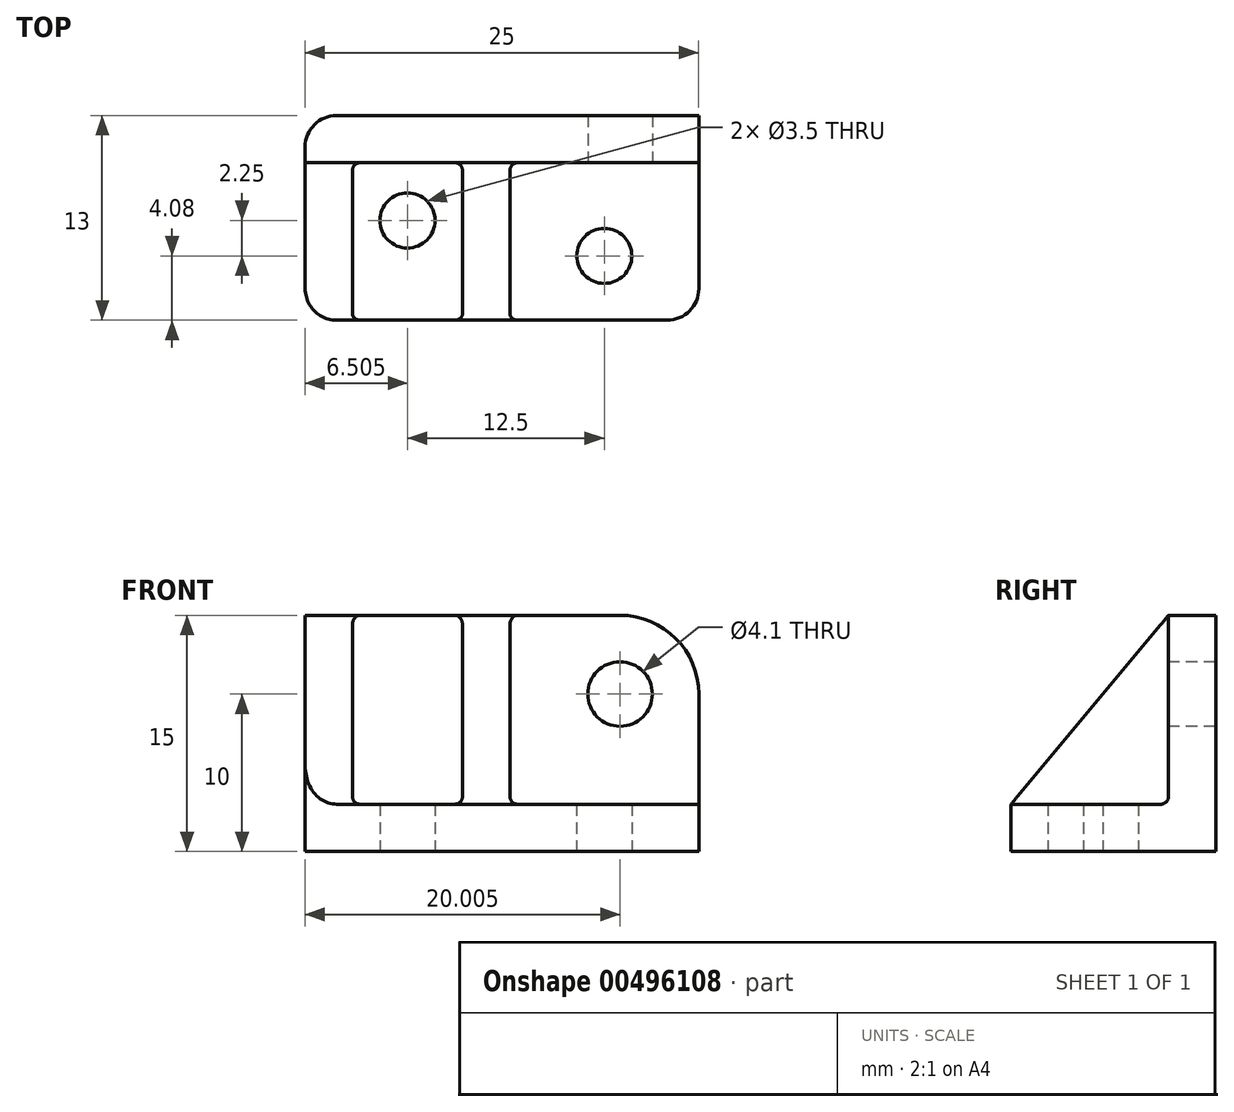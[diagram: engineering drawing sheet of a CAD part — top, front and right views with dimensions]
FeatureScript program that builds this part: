
annotation { "Feature Type Name" : "Feature", "Feature Type Description" : "" }
export const myFeature = defineFeature(function(context is Context, id is Id, definition is map)
    precondition{}
    {
        {
            var Q0;
            Q0=qCreatedBy(makeId("Top.planeOp"),FACE);
            var sketch = newSketch(context, id + "F0", { "sketchPlane" : qUnion([Q0])});
            skLineSegment(sketch, "E0.bottom", {"start": v(-68.38, 21.24) * mm, "end": v(-43.38, 21.24) * mm});
            skLineSegment(sketch, "E0.top", {"start": v(-68.38, 8.24) * mm, "end": v(-43.38, 8.24) * mm});
            skLineSegment(sketch, "E0.left", {"start": v(-68.38, 21.24) * mm, "end": v(-68.38, 8.24) * mm});
            skLineSegment(sketch, "E0.right", {"start": v(-43.38, 21.24) * mm, "end": v(-43.38, 8.24) * mm});
            skLineSegment(sketch, "E1", {"start": v(-68.38, 18.24) * mm, "end": v(-43.38, 18.24) * mm});
            skLineSegment(sketch, "E2", {"start": v(-65.38, 18.24) * mm, "end": v(-65.38, 8.24) * mm});
            skLineSegment(sketch, "E3", {"start": v(-58.38, 18.24) * mm, "end": v(-58.38, 8.24) * mm});
            skLineSegment(sketch, "E4", {"start": v(-55.38, 18.24) * mm, "end": v(-55.38, 8.24) * mm});
            skLineSegment(sketch, "E5", {"start": v(-68.38, 15.74) * mm, "end": v(-43.38, 11.24) * mm, "construction": true});
            skPoint(sketch, "E6", {"position": v(-61.88, 14.57) * mm});
            skPoint(sketch, "E7", {"position": v(-49.38, 12.32) * mm});
            skCircle(sketch, "E8", {"center": v(-61.88, 14.57) * mm, "radius": 1.75 * mm});
            skCircle(sketch, "E9", {"center": v(-49.38, 12.32) * mm, "radius": 1.75 * mm});
            skSolve(sketch);
        }
        {
            var Q0;
            {var subQ0=sQuery(id+"F0.wireOp",EDGE,"E0.bottom");Q0=makeQuery(id+"F0.imprint","IMPRINT",FACE,{"disambiguationData":[TD([[makeQuery(id+"F0.imprint","IMPRINT",EDGE,{"derivedFrom":subQ0}),-1.0]])]});}
            var Q1;
            {var subQ3=sQuery(id+"F0.wireOp",EDGE,"E2");Q1=makeQuery(id+"F0.imprint","IMPRINT",FACE,{"disambiguationData":[TD([[makeQuery(id+"F0.imprint","IMPRINT",EDGE,{"derivedFrom":subQ3}),-1.0]])]});}
            var Q2;
            {var subQ0=sQuery(id+"F0.wireOp",EDGE,"E3");Q2=makeQuery(id+"F0.imprint","IMPRINT",FACE,{"disambiguationData":[TD([[makeQuery(id+"F0.imprint","IMPRINT",EDGE,{"derivedFrom":subQ0}),1.0]])]});}
            extrude(context, id + "F1", {"entities" : qUnion([Q0, Q1, Q2]), "depth" : 15 * mm, "offsetDistance" : 25 * mm});
        }
        {
            var Q0;
            Q0 = qSketchRegion(id + "F0", true);
            extrude(context, id + "F2", {"entities" : qUnion([Q0]), "operationType" : NewBodyOperationType.ADD, "depth" : 3 * mm, "offsetDistance" : 25 * mm});
        }
        {
            var Q0;
            Q0=makeQuery(id+"F1.opExtrude","SWEPT_FACE",FACE,{"disambiguationData":[OSD([sQuery(id+"F0.wireOp",EDGE,"E1")])]});
            var sketch = newSketch(context, id + "F3", { "sketchPlane" : qUnion([Q0])});
            skCircle(sketch, "E10", {"center": v(-48.38, 10) * mm, "radius": 5 * mm});
            skCircle(sketch, "E11", {"center": v(-48.38, 10) * mm, "radius": 2.05 * mm});
            skSolve(sketch);
        }
        {
            var Q0;
            {var subQ0=sQuery(id+"F3.wireOp",EDGE,"E10");var subQ1=sQuery(id+"F0.wireOp",EDGE,"E1");var subQ2=makeQuery(id+"F1.opExtrude","CAP_EDGE",EDGE,{"disambiguationData":[OSD([subQ1])],"isStart":false});var subQ3=makeQuery(id+"F3.imprint","INTERSECT",VERTEX,{"derivedFrom":[subQ2,subQ0]});Q0=makeQuery(id+"F3.imprint","IMPRINT",FACE,{"disambiguationData":[TD([[makeQuery(id+"F3.imprint","IMPRINT",EDGE,{"disambiguationData":[TD([[subQ3,1.0]])],"derivedFrom":subQ0}),-1.0]])]});}
            var Q1;
            Q1=makeQuery(id+"F3.imprint","IMPRINT",FACE,{"disambiguationData":[TD([[makeQuery(id+"F3.imprint","IMPRINT",EDGE,{"derivedFrom":sQuery(id+"F3.wireOp",EDGE,"E11")}),1.0]])]});
            extrude(context, id + "F4", {"entities" : qUnion([Q0, Q1]), "operationType" : NewBodyOperationType.REMOVE, "oppositeDirection" : true, "depth" : 3 * mm, "offsetDistance" : 25 * mm});
        }
        {
            var Q0;
            Q0=makeQuery(id+"F1.opExtrude","SWEPT_FACE",FACE,{"disambiguationData":[OSD([sQuery(id+"F0.wireOp",EDGE,"E0.left")])]});
            var sketch = newSketch(context, id + "F5", { "sketchPlane" : qUnion([Q0])});
            skLineSegment(sketch, "E12", {"start": v(-18.24, 15) * mm, "end": v(-8.24, 3) * mm});
            skSolve(sketch);
        }
        {
            var Q0;
            {var subQ0=sQuery(id+"F5.wireOp",EDGE,"E12");Q0=makeQuery(id+"F5.imprint","IMPRINT",FACE,{"disambiguationData":[TD([[makeQuery(id+"F5.imprint","IMPRINT",EDGE,{"derivedFrom":subQ0}),1.0]])]});}
            extrude(context, id + "F6", {"entities" : qUnion([Q0]), "operationType" : NewBodyOperationType.REMOVE, "endBound" : BoundingType.THROUGH_ALL, "oppositeDirection" : true, "depth" : 50 * mm, "offsetDistance" : 25 * mm});
        }
        {
            var Q0;
            Q0=makeQuery(id+"F1.opExtrude","SWEPT_EDGE",EDGE,{"disambiguationData":[OSD([sQuery(id+"F0.wireOp",EDGE,"E0.top"),sQuery(id+"F0.wireOp",EDGE,"E0.left")])]});
            var Q1;
            Q1=makeQuery(id+"F2.opExtrude","SWEPT_EDGE",EDGE,{"disambiguationData":[OSD([sQuery(id+"F0.wireOp",EDGE,"E0.top"),sQuery(id+"F0.wireOp",EDGE,"E0.right")])]});
            var Q2;
            Q2=makeQuery(id+"F1.opExtrude","SWEPT_EDGE",EDGE,{"disambiguationData":[OSD([sQuery(id+"F0.wireOp",EDGE,"E0.bottom"),sQuery(id+"F0.wireOp",EDGE,"E0.left")])]});
            fillet(context, id + "F7", {"entities" : qUnion([Q0, Q1, Q2]), "radius" : 2 * mm, "tangentPropagation" : true, "allowEdgeOverflow" : false});
        }
        {
            var Q0;
            Q0=makeQuery(id+"F2.boolean.opBoolean","INTERSECT",EDGE,{"derivedFrom":[makeQuery(id+"F1.opExtrude","SWEPT_FACE",FACE,{"disambiguationData":[OSD([sQuery(id+"F0.wireOp",EDGE,"E4")])]}),makeQuery(id+"F2.opExtrude","CAP_FACE",FACE,{"disambiguationData":[OSD([sQuery(id+"F0.wireOp",EDGE,"E0.bottom"),sQuery(id+"F0.wireOp",EDGE,"E0.top"),sQuery(id+"F0.wireOp",EDGE,"E0.left"),sQuery(id+"F0.wireOp",EDGE,"E0.right")])],"isStart":false})]});
            var Q1;
            {var subQ0=sQuery(id+"F0.wireOp",EDGE,"E0.right");var subQ1=sQuery(id+"F0.wireOp",EDGE,"E1");Q1=makeQuery(id+"F2.boolean.opBoolean","INTERSECT",EDGE,{"derivedFrom":[makeQuery(id+"F1.opExtrude","SWEPT_FACE",FACE,{"disambiguationData":[OSD([subQ1]),TDD([makeQuery(id+"F0.imprint","IMPRINT",EDGE,{"disambiguationData":[TD([[makeQuery(id+"F0.imprint","INTERSECT",VERTEX,{"derivedFrom":[subQ0,subQ1]}),1.0]])],"derivedFrom":subQ1})])]}),makeQuery(id+"F2.opExtrude","CAP_FACE",FACE,{"disambiguationData":[OSD([sQuery(id+"F0.wireOp",EDGE,"E0.bottom"),sQuery(id+"F0.wireOp",EDGE,"E0.top"),sQuery(id+"F0.wireOp",EDGE,"E0.left"),subQ0])],"isStart":false})]});}
            var Q2;
            Q2=makeQuery(id+"F1.opExtrude","SWEPT_EDGE",EDGE,{"disambiguationData":[OSD([sQuery(id+"F0.wireOp",EDGE,"E1"),sQuery(id+"F0.wireOp",EDGE,"E4")])]});
            var Q3;
            Q3=makeQuery(id+"F2.boolean.opBoolean","INTERSECT",EDGE,{"derivedFrom":[makeQuery(id+"F1.opExtrude","SWEPT_FACE",FACE,{"disambiguationData":[OSD([sQuery(id+"F0.wireOp",EDGE,"E2")])]}),makeQuery(id+"F2.opExtrude","CAP_FACE",FACE,{"disambiguationData":[OSD([sQuery(id+"F0.wireOp",EDGE,"E0.bottom"),sQuery(id+"F0.wireOp",EDGE,"E0.top"),sQuery(id+"F0.wireOp",EDGE,"E0.left"),sQuery(id+"F0.wireOp",EDGE,"E0.right")])],"isStart":false})]});
            var Q4;
            {var subQ0=sQuery(id+"F0.wireOp",EDGE,"E1");Q4=makeQuery(id+"F2.boolean.opBoolean","INTERSECT",EDGE,{"derivedFrom":[makeQuery(id+"F1.opExtrude","SWEPT_FACE",FACE,{"disambiguationData":[OSD([subQ0]),TDD([makeQuery(id+"F0.imprint","IMPRINT",EDGE,{"disambiguationData":[TD([[makeQuery(id+"F0.imprint","INTERSECT",VERTEX,{"derivedFrom":[subQ0,sQuery(id+"F0.wireOp",EDGE,"E2")]}),-1.0]])],"derivedFrom":subQ0})])]}),makeQuery(id+"F2.opExtrude","CAP_FACE",FACE,{"disambiguationData":[OSD([sQuery(id+"F0.wireOp",EDGE,"E0.bottom"),sQuery(id+"F0.wireOp",EDGE,"E0.top"),sQuery(id+"F0.wireOp",EDGE,"E0.left"),sQuery(id+"F0.wireOp",EDGE,"E0.right")])],"isStart":false})]});}
            var Q5;
            Q5=makeQuery(id+"F1.opExtrude","SWEPT_EDGE",EDGE,{"disambiguationData":[OSD([sQuery(id+"F0.wireOp",EDGE,"E1"),sQuery(id+"F0.wireOp",EDGE,"E2")])]});
            var Q6;
            Q6=makeQuery(id+"F1.opExtrude","SWEPT_EDGE",EDGE,{"disambiguationData":[OSD([sQuery(id+"F0.wireOp",EDGE,"E1"),sQuery(id+"F0.wireOp",EDGE,"E3")])]});
            var Q7;
            Q7=makeQuery(id+"F2.boolean.opBoolean","INTERSECT",EDGE,{"derivedFrom":[makeQuery(id+"F1.opExtrude","SWEPT_FACE",FACE,{"disambiguationData":[OSD([sQuery(id+"F0.wireOp",EDGE,"E3")])]}),makeQuery(id+"F2.opExtrude","CAP_FACE",FACE,{"disambiguationData":[OSD([sQuery(id+"F0.wireOp",EDGE,"E0.bottom"),sQuery(id+"F0.wireOp",EDGE,"E0.top"),sQuery(id+"F0.wireOp",EDGE,"E0.left"),sQuery(id+"F0.wireOp",EDGE,"E0.right")])],"isStart":false})]});
            fillet(context, id + "F8", {"entities" : qUnion([Q0, Q1, Q2, Q3, Q4, Q5, Q6, Q7]), "radius" : .5 * mm, "tangentPropagation" : true, "allowEdgeOverflow" : false});
        }
    });
